# Revit family: ITK Кабельный органайзер 1U 2 боковых горизонтальных и 4 вертикальных кольца
name_source: partatom
category: Обобщенные модели
revit_build: Autodesk Revit 2016 (Build: 20160314_0715(x64)
units: mm (PartAtom-declared; Revit-internal decimal feet)

## family parameters
Всегда вертикально = Да
Может служить основой для арматурных стержней = Нет
На основе рабочей плоскости = Нет
Общий = Нет
При загрузке вырезать с полостями = Нет
Размер круглого соединителя = Использовать диаметр
Тип детали = Нормальный
Точка расчета площади = Нет

## types (2) — shared parameters
ADSK_Группирование = I. ЩИТЫ И ПУЛЬТЫ
ADSK_Единица измерения = шт
ADSK_Завод-изготовитель = IEK
URL = http://www.itk-group.ru
Высота = 45 мм
Глубина = 12 мм
Изготовитель = ITK
Описание = 19-дюймовые кабельные организаторы ITK предназначены для горизонтальной организации кабеля и кабельных пучков в шкафах и стойках для укладки кабелей в пространствах между коммутационными панелями и установленным активным оборудованием, обеспечивают их поддержку в пределах монтажной высоты шкафа, гарантируют необходимый радиус изгиба коммутационных шнуров и кабеля при подведении их к оборудованию, позволяют избежать перекручивания и спутывания кабелей. При использовании кабельных организаторов существенно снижается вероятность появления сильных перегибов и изломов кабелей, повышается скорость и эффективность работы IT-специалистов и администраторов при обслуживании шкафов и стоек.

Кабельные органайзеры устанавливаются на 19-дюймовые монтажные профили, занимая при этом один или два юнита полезной высоты. Монтаж осуществляется с помощью крепежа винт-шайба-гайка.

Горизонтальные кабельные организаторы представлены двумя основными видами: открытый органайзер с кольцами или закрытого типа с крышкой. Высота органайзеров: 1U или 2U. Материал: листовая сталь. В комплект поставки входит органайзер и комплект крепежа.
Совместимы со всеми 19-дюймовыми шкафами и стойками ITK.
Обладают современным привлекательным дизайном и продуманной конструкцией.
Удобны в монтаже и эксплуатации.
Соответствие международным стандартам ISO9001, IEC 297, ISO/IEC 11801. 
Сертифицированы по ГОСТ Р.
Все аксессуары идут с крепежом.
Возможно исполнение в двух цветах: серый (RAL7035) и черный (RAL9005).
Всегда в наличии на складе.
Гарантия на все аксессуары до 2-х лет.
Ширина = 483 мм
zero-valued in all types: ADSK_Масса

## per-type parameters (varying)
| type | ADSK_Наименование | Материал |
| CO05-1M6R | ITK Кабельный органайзер 1U 2 боковых горизонтальных и 4 вертикальных кольца, черный | Окраска - RAL 9005 |
| CO35-1M6R | ITK Кабельный органайзер 1U 2 боковых горизонтальных и 4 вертикальных кольца, серый | Окраска - RAL 7035 |

note: column(s) folded — value = type name in every type: ADSK_Марка, ADSK_Наименование краткое
